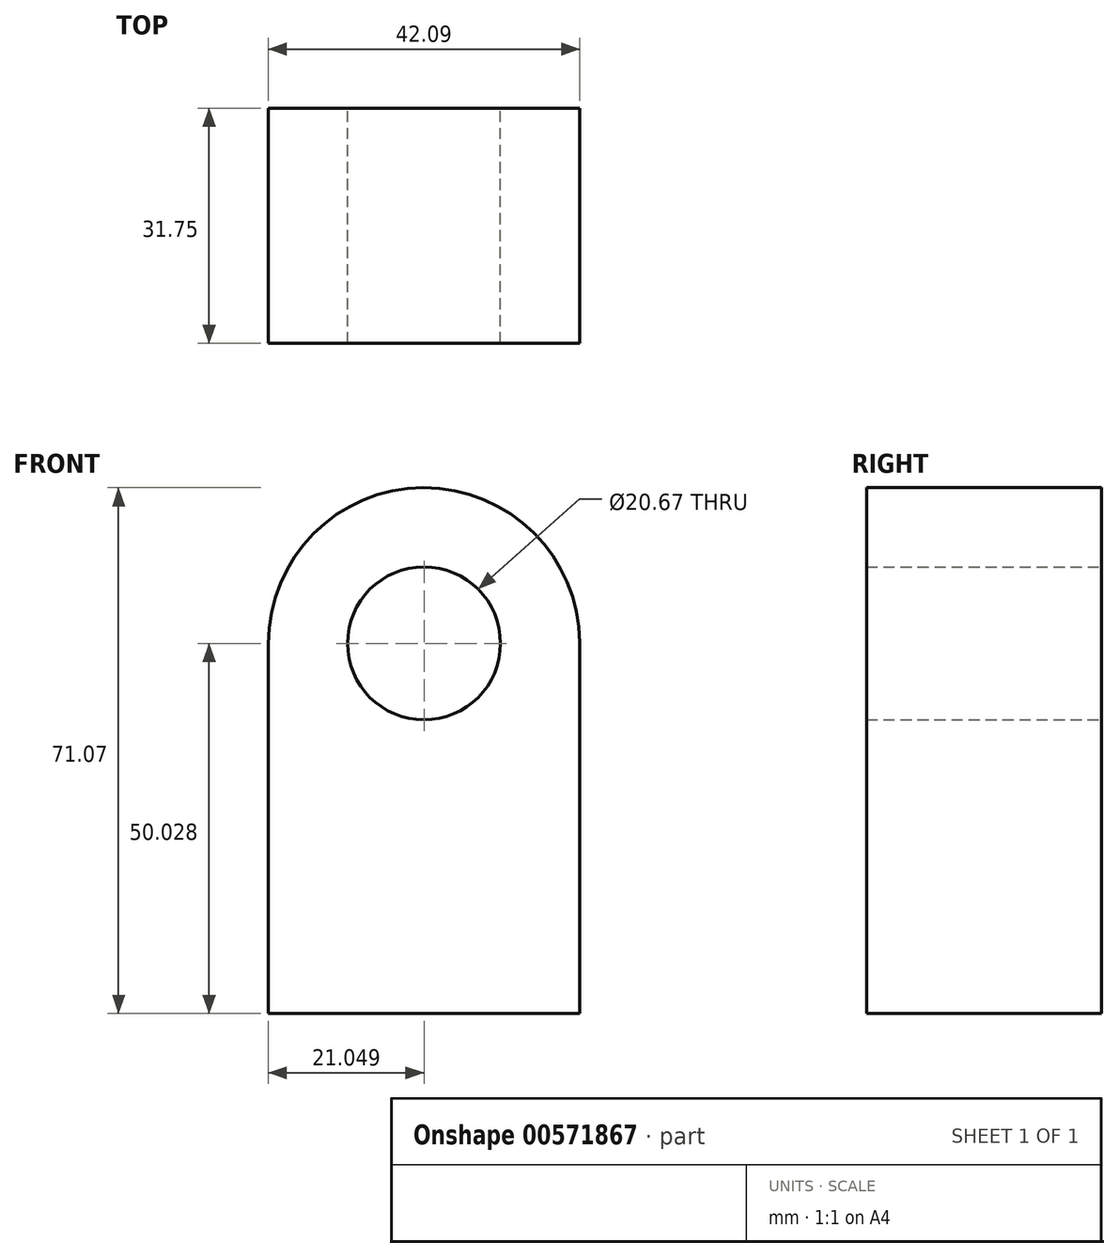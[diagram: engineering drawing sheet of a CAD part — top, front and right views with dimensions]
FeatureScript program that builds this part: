
annotation { "Feature Type Name" : "Feature", "Feature Type Description" : "" }
export const myFeature = defineFeature(function(context is Context, id is Id, definition is map)
    precondition{}
    {
        {
            var Q0;
            Q0=qCreatedBy(makeId("Front.planeOp"),FACE);
            var sketch = newSketch(context, id + "F0", { "sketchPlane" : qUnion([Q0])});
            skLineSegment(sketch, "E0", {"start": v(-55.24, 58.58) * mm, "end": v(-55.24, 8.62) * mm});
            skLineSegment(sketch, "E1", {"start": v(-55.24, 8.62) * mm, "end": v(-13.15, 8.62) * mm});
            skLineSegment(sketch, "E2", {"start": v(-13.15, 8.62) * mm, "end": v(-13.15, 58.72) * mm});
            skCircle(sketch, "E3", {"center": v(-34.2, 58.65) * mm, "radius": 10.34 * mm});
            skArc(sketch, "E4", {"start": v(-13.15, 58.72) * mm, "mid": v(-34.26, 79.7) * mm, "end": v(-55.24, 58.58) * mm});
            skSolve(sketch);
        }
        {
            var Q0;
            Q0=makeQuery(id+"F0.imprint","IMPRINT",FACE,{"disambiguationData":[TD([[makeQuery(id+"F0.imprint","IMPRINT",EDGE,{"derivedFrom":sQuery(id+"F0.wireOp",EDGE,"E0")}),1.0]])]});
            extrude(context, id + "F1", {"entities" : qUnion([Q0]), "depth" : 31.75 * mm, "offsetDistance" : 25.4 * mm});
        }
    });
